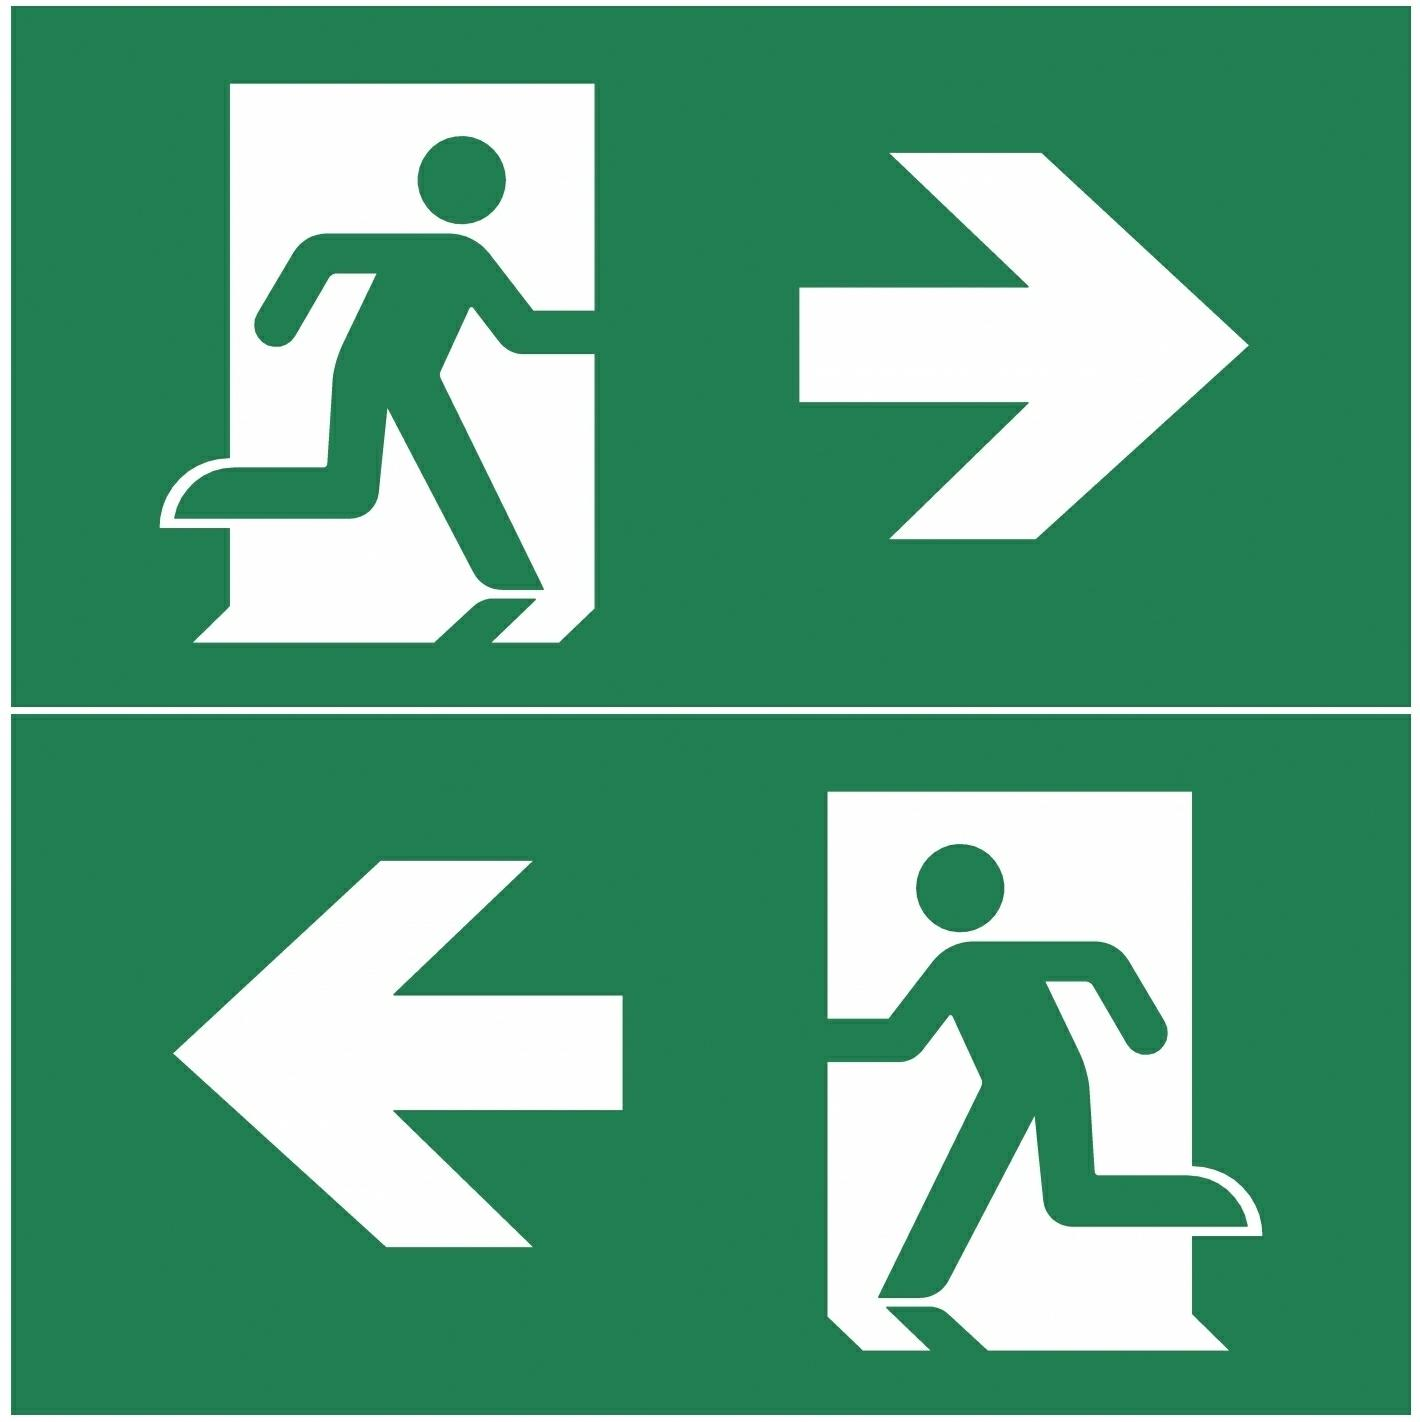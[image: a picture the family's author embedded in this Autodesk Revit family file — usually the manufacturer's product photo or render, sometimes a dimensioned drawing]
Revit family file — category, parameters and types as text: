
# Revit family: TWT8053WA
name_source: partatom
category: Lighting Fixtures
revit_build: Autodesk Revit 2016 (Build: 20150714_1515(x64)
units: mm (PartAtom-declared; Revit-internal decimal feet)

## family parameters
Always vertical = Yes
Cut with Voids When Loaded = No
Light Source = No
OmniClass Number = 23.80.70.00
OmniClass Title = Lighting
Part Type = Normal
Room Calculation Point = No
Round Connector Dimension = Use Diameter
Shared = No
Work Plane-Based = No

## types (6) — shared parameters
Body Material = Plastic
Color = RAL9003
Customs Code = 94056080
Description = Self-Contained LED Exit Light with 3 h Battery Backup and Wireless Monitoring
ETIM Product Class = EC001957
Electrical Installation = 2/3 x 2,5 mm² -o-
Feature = Aalto Control
Glow Wire Test of Plastic Materials = 650 °C
Height = 185 mm  [stored 0.606955 ft]
IP Class = IP44
Keynote = 23
Length = 268 mm  [stored 0.879265 ft]
Light Source = LED
Manufacturer = Teknoware Oy
Max Input Power VA = 5 VA
Model = ESC 80
Mounting_Optional = Recess, Flag, Pendel
Mounting_Standard = Wall, Ceiling
Nominal Supply Voltage = 220-240 V, 50/60 Hz AC
Product Code = TWT8053WA
Protection Class = II
Sähkönumero = 4211317
Sähkönumerot.fi -tuotesivu = http://www.sahkonumerot.fi
Temperature Range Min_Max = -5...+30 °C
Type Image = ESC80.jpg
URL = http://www.teknoware.com
Viewing Distance = 20000 mm  [stored 65.6168 ft]
Wattage Comments = LED
Weight = 0.74 kg
Width = 40 mm  [stored 0.131234 ft]

## per-type parameters (varying)
| type | Aperture for Recess Mounting | GTIN Code | Max Input Power W | Pictogram Type |
| Arrow down 20m | 53 mm x 275 mm | 6438045011837 | 4 W | OPASTE PBV80202E |
| Arrow down 30m | 53 mm  x 275 mm | 6438045011837 | 0 W | OPASTE PBV80302E |
| Arrow down 26m | 53 mm x 275 mm | 6438045011837 | 4 W | OPASTE PBV80262E |
| Arrow left_right 20m | 53 mm x 275 mm | 6438045011837 | 4 W | OPASTE PBV80201E |
| Arrow left_right 26m | 53 mm x 275 mm | 6438045011813 | 4 W | OPASTE PBV80261E |
| Arrow left_right 30m | 53 mm x 275 mm | 6438045011837 | 4 W | OPASTE PBV80301E |

note: [stored X ft] marks values corroborated as IEEE doubles in the binary element streams (Revit-internal decimal feet)

## geometry (parser evidence)
native form markers: Sweep x24
no freeform markers — native parametric forms only
